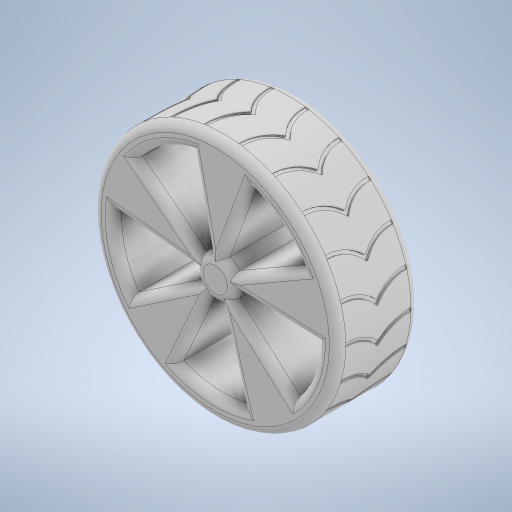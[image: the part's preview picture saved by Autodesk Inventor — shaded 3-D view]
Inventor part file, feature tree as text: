
AUTODESK INVENTOR PART (.ipt)
format: ipt  version: 2023 (Build 270158000, 158)  size: 830,464 bytes
history: native  units: in
note: dims shown in document units (in); Inventor stores cm internally (conversion verified against a paired STEP export)
features: extrude x3, sketch x3, fillet x2, pattern_circular x2, plane x1, projected_geometry x1
ambient origin geometry x8: Origin, YZ Plane, XZ Plane, XY Plane, X Axis, Y Axis, Z Axis, Center Point
bodies: Solid1 (feature_tree)
feature tree (12):
  extrude  "Extrusion1"  Depth=0.7874in TaperAngle=0.0deg
  fillet  "Fillet1"  Radius=0.0787in
  extrude  "Extrusion2"  Depth=0.3937in
  pattern_circular  "Circular Pattern1"  [2 undecoded]
  fillet  "Fillet2"  Radius=1.9685in
  plane  "Work Plane1"
  extrude  "Extrusion3"  Depth=0.3937in
  pattern_circular  "Circular Pattern2"  Count=3  [1 undecoded]
  sketch  "Sketch2"  dims[d0=2.3622in d1=0.7874in d2=0.0in d3=0.0787in]
  sketch  "Sketch3"  dims[d4=0.3937in d5=1.9685in]
  sketch  "Sketch4"  dims[d6=30.0deg d7=0.3937in d8=0.0in d9=1.9685in d10=360.0deg d12=0.0787in d13=1.1811in d17=0.0197in d18=0.0in d19=8.6614in d20=360.0deg]
  projected_geometry  "Projected Loop1"
note: 3 required parameter values undecoded (feature->parameter linkage not recoverable at this tier; creation-order binding heuristic only, values carry confidence <= 0.55)
